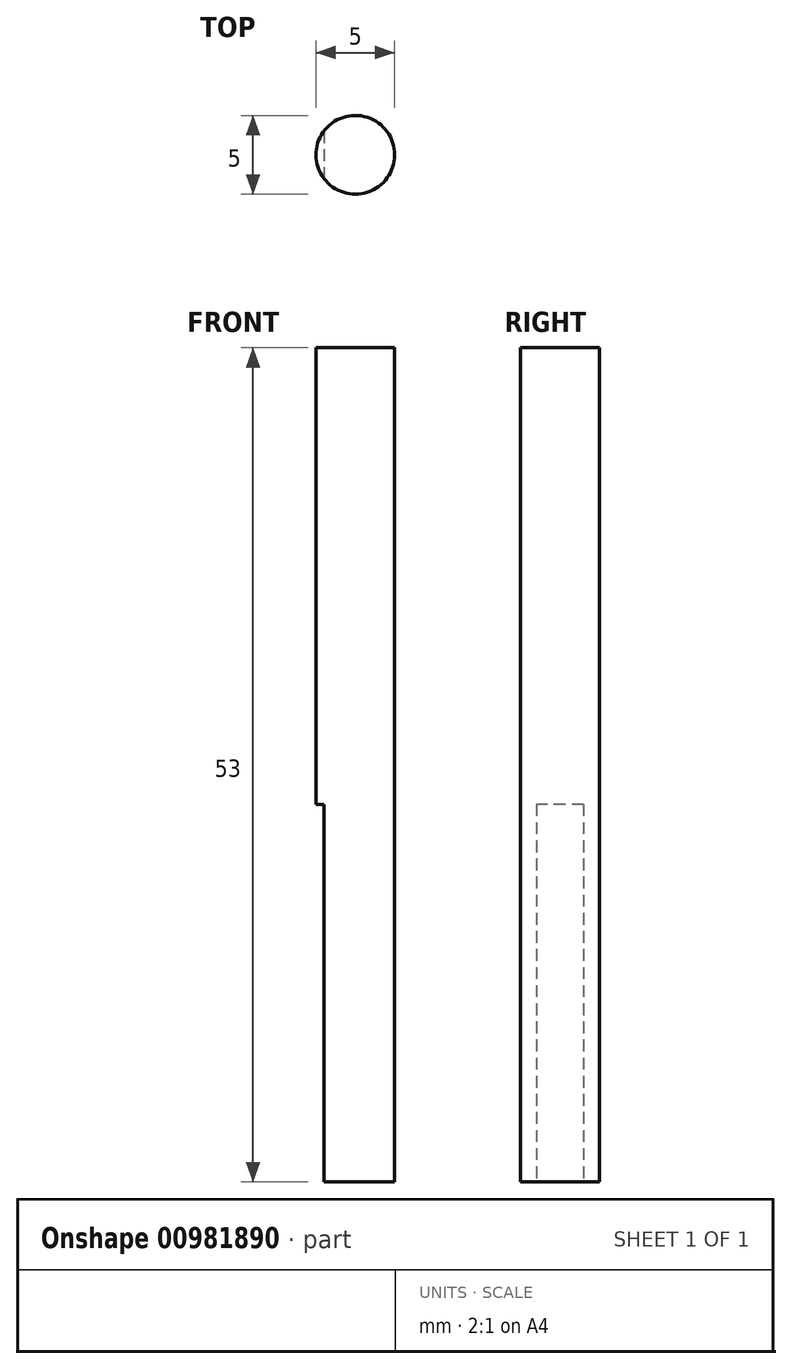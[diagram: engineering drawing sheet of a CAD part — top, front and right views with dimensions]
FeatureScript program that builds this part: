
annotation { "Feature Type Name" : "Feature", "Feature Type Description" : "" }
export const myFeature = defineFeature(function(context is Context, id is Id, definition is map)
    precondition{}
    {
        {
            var Q0;
            Q0=qCreatedBy(makeId("Top.planeOp"),FACE);
            var sketch = newSketch(context, id + "F0", { "sketchPlane" : qUnion([Q0])});
            skCircle(sketch, "E0", {"center": v(-25.54, 13.44) * mm, "radius": 2.5 * mm});
            skLineSegment(sketch, "E1", {"start": v(-23.04, 13.44) * mm, "end": v(-27.54, 13.44) * mm, "construction": true});
            skLineSegment(sketch, "E2", {"start": v(-27.54, 13.44) * mm, "end": v(-27.54, 14.94) * mm, "construction": true});
            skLineSegment(sketch, "E3", {"start": v(-27.54, 14.94) * mm, "end": v(-27.54, 11.94) * mm, "construction": true});
            skLineSegment(sketch, "E4", {"start": v(-27.54, 14.94) * mm, "end": v(-27.54, 11.94) * mm});
            skSolve(sketch);
        }
        {
            var Q0;
            Q0=makeQuery(id+"F0.imprint","IMPRINT",FACE,{"disambiguationData":[TD([[makeQuery(id+"F0.imprint","IMPRINT",EDGE,{"derivedFrom":sQuery(id+"F0.wireOp",EDGE,"E0")}),1.0]])]});
            extrude(context, id + "F1", {"entities" : qUnion([Q0]), "depth" : 53 * mm, "offsetDistance" : 25 * mm});
        }
        {
            var Q0;
            {var subQ0=sQuery(id+"F0.wireOp",EDGE,"E4");Q0=makeQuery(id+"F0.imprint","IMPRINT",FACE,{"disambiguationData":[TD([[makeQuery(id+"F0.imprint","IMPRINT",EDGE,{"derivedFrom":subQ0}),-1.0]])]});}
            extrude(context, id + "F2", {"entities" : qUnion([Q0]), "operationType" : NewBodyOperationType.REMOVE, "depth" : 24 * mm, "offsetDistance" : 25 * mm});
        }
    });
